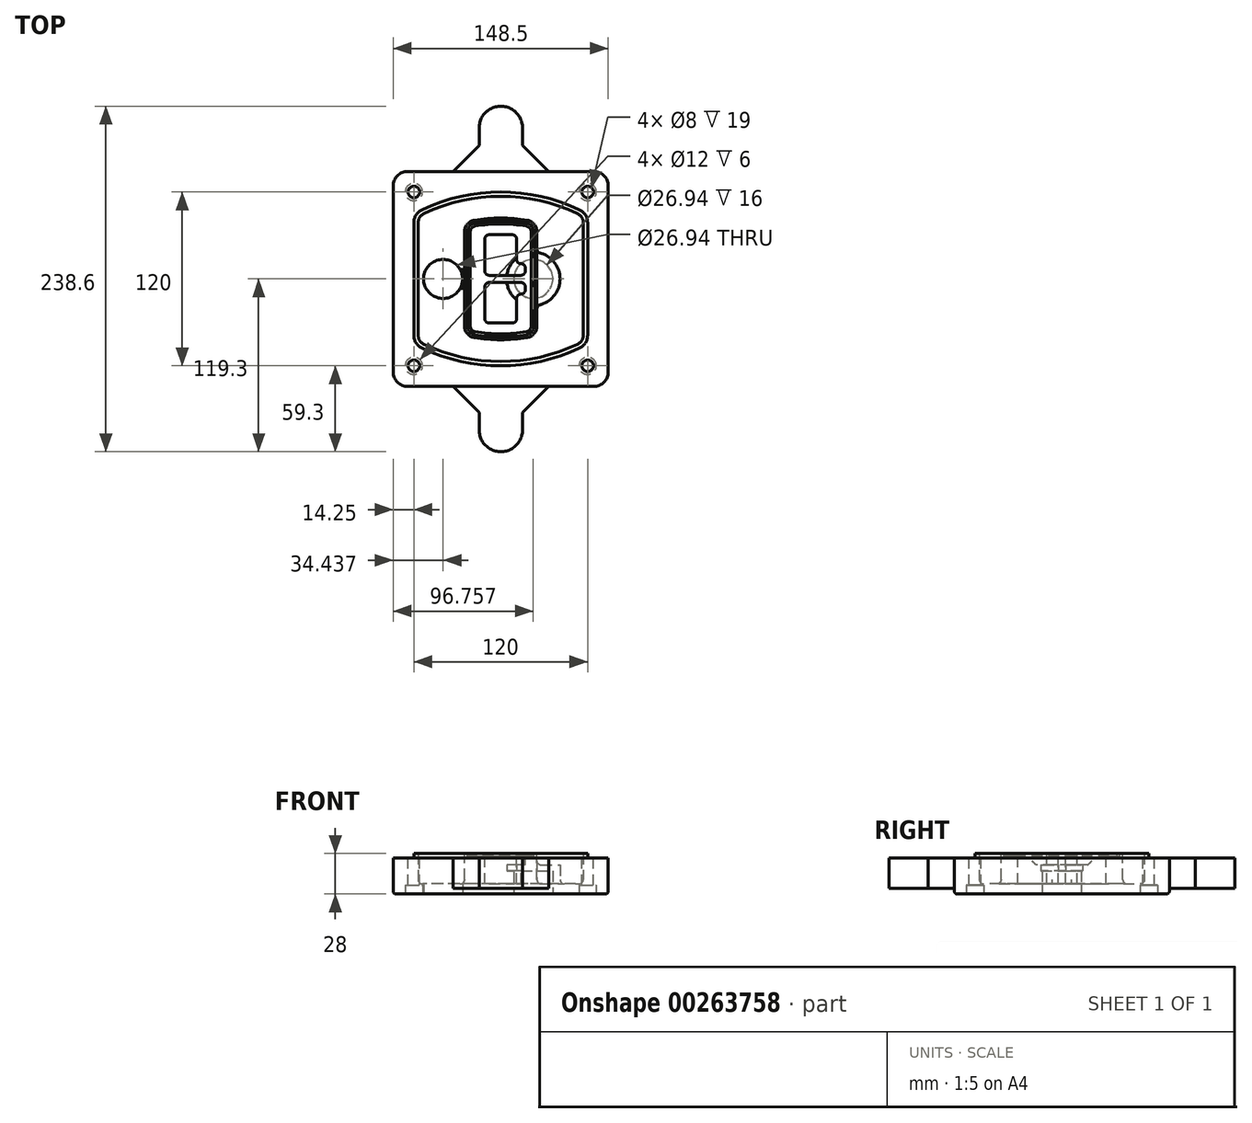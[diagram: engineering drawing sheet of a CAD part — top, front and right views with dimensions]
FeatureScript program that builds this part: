
annotation { "Feature Type Name" : "Feature", "Feature Type Description" : "" }
export const myFeature = defineFeature(function(context is Context, id is Id, definition is map)
    precondition{}
    {
        {
            var Q0;
            Q0=qCreatedBy(makeId("Top.planeOp"),FACE);
            var sketch = newSketch(context, id + "F0", { "sketchPlane" : qUnion([Q0])});
            skPoint(sketch, "E0.rect.middle", {"position": v(0, 0) * mm});
            skLineSegment(sketch, "E1.bottom", {"start": v(-64.25, -74.25) * mm, "end": v(64.25, -74.25) * mm});
            skLineSegment(sketch, "E1.top", {"start": v(-64.25, 74.25) * mm, "end": v(64.25, 74.25) * mm});
            skLineSegment(sketch, "E1.left", {"start": v(-74.25, -64.25) * mm, "end": v(-74.25, 64.25) * mm});
            skLineSegment(sketch, "E1.right", {"start": v(74.25, -64.25) * mm, "end": v(74.25, 64.25) * mm});
            skLineSegment(sketch, "E2", {"start": v(-74.25, 74.25) * mm, "end": v(74.25, -74.25) * mm, "construction": true});
            skLineSegment(sketch, "E3", {"start": v(74.25, 74.25) * mm, "end": v(-74.25, -74.25) * mm, "construction": true});
            skCircle(sketch, "E4", {"center": v(-60, 60) * mm, "radius": 4 * mm});
            skCircle(sketch, "E5", {"center": v(60, 60) * mm, "radius": 4 * mm});
            skCircle(sketch, "E6", {"center": v(60, -60) * mm, "radius": 4 * mm});
            skCircle(sketch, "E7", {"center": v(-60, -60) * mm, "radius": 4 * mm});
            skLineSegment(sketch, "E8", {"start": v(-60, 60) * mm, "end": v(60, 60) * mm, "construction": true});
            skLineSegment(sketch, "E9", {"start": v(60, 60) * mm, "end": v(60, -60) * mm, "construction": true});
            skLineSegment(sketch, "E10", {"start": v(60, -60) * mm, "end": v(-60, -60) * mm, "construction": true});
            skLineSegment(sketch, "E11", {"start": v(-60, -60) * mm, "end": v(-60, 60) * mm, "construction": true});
            skLineSegment(sketch, "E12", {"start": v(-60, 38.83) * mm, "end": v(-60, -38.83) * mm});
            skLineSegment(sketch, "E13", {"start": v(60, 38.83) * mm, "end": v(60, -38.83) * mm});
            skArc(sketch, "E14", {"start": v(54.26, 47.88) * mm, "mid": v(0, 60) * mm, "end": v(-54.26, 47.88) * mm});
            skArc(sketch, "E15", {"start": v(-54.26, -47.88) * mm, "mid": v(0, -60) * mm, "end": v(54.26, -47.88) * mm});
            skLineSegment(sketch, "E16", {"start": v(-60, 0) * mm, "end": v(60, 0) * mm, "construction": true});
            skPoint(sketch, "E17.visualSharp", {"position": v(-60, -45) * mm});
            skArc(sketch, "E17.filletArc", {"start": v(-60, -38.83) * mm, "mid": v(-58.44, -44.2) * mm, "end": v(-54.26, -47.88) * mm});
            skPoint(sketch, "E18.visualSharp", {"position": v(-60, 45) * mm});
            skArc(sketch, "E18.filletArc", {"start": v(-54.26, 47.88) * mm, "mid": v(-58.44, 44.2) * mm, "end": v(-60, 38.83) * mm});
            skPoint(sketch, "E19.visualSharp", {"position": v(60, 45) * mm});
            skArc(sketch, "E19.filletArc", {"start": v(60, 38.83) * mm, "mid": v(58.44, 44.2) * mm, "end": v(54.26, 47.88) * mm});
            skPoint(sketch, "E20.visualSharp", {"position": v(60, -45) * mm});
            skArc(sketch, "E20.filletArc", {"start": v(54.26, -47.88) * mm, "mid": v(58.44, -44.2) * mm, "end": v(60, -38.83) * mm});
            skPoint(sketch, "E21.visualSharp", {"position": v(-74.25, 74.25) * mm});
            skArc(sketch, "E21.filletArc", {"start": v(-64.25, 74.25) * mm, "mid": v(-71.32, 71.32) * mm, "end": v(-74.25, 64.25) * mm});
            skPoint(sketch, "E22.visualSharp", {"position": v(74.25, 74.25) * mm});
            skArc(sketch, "E22.filletArc", {"start": v(74.25, 64.25) * mm, "mid": v(71.32, 71.32) * mm, "end": v(64.25, 74.25) * mm});
            skPoint(sketch, "E23.visualSharp", {"position": v(74.25, -74.25) * mm});
            skArc(sketch, "E23.filletArc", {"start": v(64.25, -74.25) * mm, "mid": v(71.32, -71.32) * mm, "end": v(74.25, -64.25) * mm});
            skPoint(sketch, "E24.visualSharp", {"position": v(-74.25, -74.25) * mm});
            skArc(sketch, "E24.filletArc", {"start": v(-74.25, -64.25) * mm, "mid": v(-71.32, -71.32) * mm, "end": v(-64.25, -74.25) * mm});
            skArc(sketch, "E25.0", {"start": v(57, 38.83) * mm, "mid": v(55.9, 42.58) * mm, "end": v(52.98, 45.17) * mm});
            skLineSegment(sketch, "E25.1", {"start": v(57, 38.83) * mm, "end": v(57, -38.83) * mm});
            skArc(sketch, "E25.2", {"start": v(52.98, -45.17) * mm, "mid": v(55.9, -42.58) * mm, "end": v(57, -38.83) * mm});
            skArc(sketch, "E25.3", {"start": v(-52.98, -45.17) * mm, "mid": v(0, -57) * mm, "end": v(52.98, -45.17) * mm});
            skArc(sketch, "E25.4", {"start": v(-57, -38.83) * mm, "mid": v(-55.9, -42.58) * mm, "end": v(-52.98, -45.17) * mm});
            skArc(sketch, "E25.5", {"start": v(52.98, 45.17) * mm, "mid": v(0, 57) * mm, "end": v(-52.98, 45.17) * mm});
            skLineSegment(sketch, "E25.6", {"start": v(-57, 38.83) * mm, "end": v(-57, -38.83) * mm});
            skArc(sketch, "E25.7", {"start": v(-52.98, 45.17) * mm, "mid": v(-55.9, 42.58) * mm, "end": v(-57, 38.83) * mm});
            skArc(sketch, "E26.0", {"start": v(-55.96, 51.5) * mm, "mid": v(-61.82, 46.33) * mm, "end": v(-64, 38.83) * mm});
            skArc(sketch, "E26.1", {"start": v(55.96, 51.5) * mm, "mid": v(0, 64) * mm, "end": v(-55.96, 51.5) * mm});
            skArc(sketch, "E26.2", {"start": v(64, 38.83) * mm, "mid": v(61.82, 46.33) * mm, "end": v(55.96, 51.5) * mm});
            skLineSegment(sketch, "E26.3", {"start": v(64, 38.83) * mm, "end": v(64, -38.83) * mm});
            skArc(sketch, "E26.4", {"start": v(55.96, -51.5) * mm, "mid": v(61.82, -46.33) * mm, "end": v(64, -38.83) * mm});
            skLineSegment(sketch, "E26.5", {"start": v(-64, 38.83) * mm, "end": v(-64, -38.83) * mm});
            skArc(sketch, "E26.6", {"start": v(-55.96, -51.5) * mm, "mid": v(0, -64) * mm, "end": v(55.96, -51.5) * mm});
            skArc(sketch, "E26.7", {"start": v(-64, -38.83) * mm, "mid": v(-61.82, -46.33) * mm, "end": v(-55.96, -51.5) * mm});
            skSolve(sketch);
        }
        {
            var Q0;
            Q0=makeQuery(id+"F0.imprint","IMPRINT",FACE,{"disambiguationData":[TD([[makeQuery(id+"F0.imprint","IMPRINT",EDGE,{"derivedFrom":sQuery(id+"F0.wireOp",EDGE,"E1.bottom")}),1.0]])]});
            var Q1;
            Q1=makeQuery(id+"F0.imprint","IMPRINT",FACE,{"disambiguationData":[TD([[makeQuery(id+"F0.imprint","IMPRINT",EDGE,{"derivedFrom":sQuery(id+"F0.wireOp",EDGE,"E12")}),1.0]])]});
            var Q2;
            Q2=makeQuery(id+"F0.imprint","IMPRINT",FACE,{"disambiguationData":[TD([[makeQuery(id+"F0.imprint","IMPRINT",EDGE,{"derivedFrom":sQuery(id+"F0.wireOp",EDGE,"E25.0")}),1.0]])]});
            var Q3;
            Q3=makeQuery(id+"F0.imprint","IMPRINT",FACE,{"disambiguationData":[TD([[makeQuery(id+"F0.imprint","IMPRINT",EDGE,{"derivedFrom":sQuery(id+"F0.wireOp",EDGE,"E12")}),-1.0]])]});
            extrude(context, id + "F1", {"entities" : qUnion([Q0, Q1, Q2, Q3]), "oppositeDirection" : true, "depth" : 25 * mm});
        }
        {
            var Q0;
            Q0=makeQuery(id+"F0.imprint","IMPRINT",FACE,{"disambiguationData":[TD([[makeQuery(id+"F0.imprint","IMPRINT",EDGE,{"derivedFrom":sQuery(id+"F0.wireOp",EDGE,"E12")}),1.0]])]});
            extrude(context, id + "F2", {"entities" : qUnion([Q0]), "operationType" : NewBodyOperationType.ADD, "depth" : 3 * mm});
        }
        {
            var Q0;
            Q0=makeQuery(id+"F0.imprint","IMPRINT",FACE,{"disambiguationData":[TD([[makeQuery(id+"F0.imprint","IMPRINT",EDGE,{"derivedFrom":sQuery(id+"F0.wireOp",EDGE,"E25.0")}),1.0]])]});
            extrude(context, id + "F3", {"entities" : qUnion([Q0]), "operationType" : NewBodyOperationType.REMOVE, "oppositeDirection" : true, "depth" : 18 * mm});
        }
        {
            var Q0;
            Q0=makeQuery(id+"F2.opExtrude","CAP_FACE",FACE,{"disambiguationData":[OSD([sQuery(id+"F0.wireOp",EDGE,"E12"),sQuery(id+"F0.wireOp",EDGE,"E13"),sQuery(id+"F0.wireOp",EDGE,"E14"),sQuery(id+"F0.wireOp",EDGE,"E15"),sQuery(id+"F0.wireOp",EDGE,"E17.filletArc"),sQuery(id+"F0.wireOp",EDGE,"E18.filletArc"),sQuery(id+"F0.wireOp",EDGE,"E19.filletArc"),sQuery(id+"F0.wireOp",EDGE,"E20.filletArc"),sQuery(id+"F0.wireOp",EDGE,"E25.0"),sQuery(id+"F0.wireOp",EDGE,"E25.1"),sQuery(id+"F0.wireOp",EDGE,"E25.2"),sQuery(id+"F0.wireOp",EDGE,"E25.3"),sQuery(id+"F0.wireOp",EDGE,"E25.4"),sQuery(id+"F0.wireOp",EDGE,"E25.5"),sQuery(id+"F0.wireOp",EDGE,"E25.6"),sQuery(id+"F0.wireOp",EDGE,"E25.7")])],"isStart":false});
            var sketch = newSketch(context, id + "F4", { "sketchPlane" : qUnion([Q0])});
            skArc(sketch, "E27.0", {"start": v(-18.34, -40.45) * mm, "mid": v(0, -42) * mm, "end": v(18.34, -40.45) * mm});
            skArc(sketch, "E28.0", {"start": v(18.34, 40.45) * mm, "mid": v(0, 42) * mm, "end": v(-18.34, 40.45) * mm});
            skLineSegment(sketch, "E29", {"start": v(-25, 32.57) * mm, "end": v(-25, -32.57) * mm});
            skLineSegment(sketch, "E30", {"start": v(25, 32.57) * mm, "end": v(25, -32.57) * mm});
            skLineSegment(sketch, "E31", {"start": v(-25, 39.1) * mm, "end": v(25, 39.1) * mm, "construction": true});
            skLineSegment(sketch, "E32", {"start": v(-25, -39.1) * mm, "end": v(25, -39.1) * mm, "construction": true});
            skPoint(sketch, "E33.visualSharp", {"position": v(-25, 39.1) * mm});
            skArc(sketch, "E33.filletArc", {"start": v(-18.34, 40.45) * mm, "mid": v(-23.11, 37.73) * mm, "end": v(-25, 32.57) * mm});
            skPoint(sketch, "E34.visualSharp", {"position": v(25, 39.1) * mm});
            skArc(sketch, "E34.filletArc", {"start": v(25, 32.57) * mm, "mid": v(23.11, 37.73) * mm, "end": v(18.34, 40.45) * mm});
            skPoint(sketch, "E35.visualSharp", {"position": v(25, -39.1) * mm});
            skArc(sketch, "E35.filletArc", {"start": v(18.34, -40.45) * mm, "mid": v(23.11, -37.73) * mm, "end": v(25, -32.57) * mm});
            skPoint(sketch, "E36.visualSharp", {"position": v(-25, -39.1) * mm});
            skArc(sketch, "E36.filletArc", {"start": v(-25, -32.57) * mm, "mid": v(-23.11, -37.73) * mm, "end": v(-18.34, -40.45) * mm});
            skArc(sketch, "E37.0", {"start": v(52.98, 45.17) * mm, "mid": v(0, 57) * mm, "end": v(-52.98, 45.17) * mm});
            skArc(sketch, "E37.1", {"start": v(-52.98, 45.17) * mm, "mid": v(-55.9, 42.58) * mm, "end": v(-57, 38.83) * mm});
            skLineSegment(sketch, "E37.2", {"start": v(-57, 38.83) * mm, "end": v(-57, -38.83) * mm});
            skArc(sketch, "E37.3", {"start": v(-57, -38.83) * mm, "mid": v(-55.9, -42.58) * mm, "end": v(-52.98, -45.17) * mm});
            skArc(sketch, "E37.4", {"start": v(-52.98, -45.17) * mm, "mid": v(0, -57) * mm, "end": v(52.98, -45.17) * mm});
            skArc(sketch, "E37.5", {"start": v(52.98, -45.17) * mm, "mid": v(55.9, -42.58) * mm, "end": v(57, -38.83) * mm});
            skLineSegment(sketch, "E37.6", {"start": v(57, 38.83) * mm, "end": v(57, -38.83) * mm});
            skArc(sketch, "E37.7", {"start": v(57, 38.83) * mm, "mid": v(55.9, 42.58) * mm, "end": v(52.98, 45.17) * mm});
            skLineSegment(sketch, "E38.0", {"start": v(23, 32.57) * mm, "end": v(23, -32.57) * mm});
            skArc(sketch, "E38.1", {"start": v(18, -38.48) * mm, "mid": v(21.58, -36.44) * mm, "end": v(23, -32.57) * mm});
            skArc(sketch, "E38.2", {"start": v(-18, -38.48) * mm, "mid": v(0, -40) * mm, "end": v(18, -38.48) * mm});
            skArc(sketch, "E38.3", {"start": v(-23, -32.57) * mm, "mid": v(-21.58, -36.44) * mm, "end": v(-18, -38.48) * mm});
            skLineSegment(sketch, "E38.4", {"start": v(-23, 32.57) * mm, "end": v(-23, -32.57) * mm});
            skArc(sketch, "E38.5", {"start": v(23, 32.57) * mm, "mid": v(21.58, 36.44) * mm, "end": v(18, 38.48) * mm});
            skArc(sketch, "E38.6", {"start": v(-18, 38.48) * mm, "mid": v(-21.58, 36.44) * mm, "end": v(-23, 32.57) * mm});
            skArc(sketch, "E38.7", {"start": v(18, 38.48) * mm, "mid": v(0, 40) * mm, "end": v(-18, 38.48) * mm});
            skArc(sketch, "E39.0", {"start": v(21, 32.57) * mm, "mid": v(20.06, 35.15) * mm, "end": v(17.67, 36.5) * mm});
            skLineSegment(sketch, "E39.1", {"start": v(21, 32.57) * mm, "end": v(21, -32.57) * mm});
            skArc(sketch, "E39.2", {"start": v(17.67, -36.5) * mm, "mid": v(20.06, -35.15) * mm, "end": v(21, -32.57) * mm});
            skArc(sketch, "E39.3", {"start": v(-17.67, -36.5) * mm, "mid": v(0, -38) * mm, "end": v(17.67, -36.5) * mm});
            skArc(sketch, "E39.4", {"start": v(-21, -32.57) * mm, "mid": v(-20.06, -35.15) * mm, "end": v(-17.67, -36.5) * mm});
            skArc(sketch, "E39.5", {"start": v(17.67, 36.5) * mm, "mid": v(0, 38) * mm, "end": v(-17.67, 36.5) * mm});
            skLineSegment(sketch, "E39.6", {"start": v(-21, 32.57) * mm, "end": v(-21, -32.57) * mm});
            skArc(sketch, "E39.7", {"start": v(-17.67, 36.5) * mm, "mid": v(-20.06, 35.15) * mm, "end": v(-21, 32.57) * mm});
            skLineSegment(sketch, "E40", {"start": v(-25, 0) * mm, "end": v(25, 0) * mm, "construction": true});
            skLineSegment(sketch, "E41", {"start": v(-11, 5.5) * mm, "end": v(-11, 27.5) * mm});
            skLineSegment(sketch, "E42", {"start": v(-8, 30.5) * mm, "end": v(8, 30.5) * mm});
            skLineSegment(sketch, "E43", {"start": v(11, 27.5) * mm, "end": v(11, 13.5) * mm});
            skLineSegment(sketch, "E44", {"start": v(14, 10.5) * mm, "end": v(14, 10.5) * mm});
            skLineSegment(sketch, "E45", {"start": v(17, 7.5) * mm, "end": v(17, 5.5) * mm});
            skLineSegment(sketch, "E46", {"start": v(14, 2.5) * mm, "end": v(-8, 2.5) * mm});
            skPoint(sketch, "E47.visualSharp", {"position": v(-11, 30.5) * mm});
            skArc(sketch, "E47.filletArc", {"start": v(-8, 30.5) * mm, "mid": v(-10.12, 29.62) * mm, "end": v(-11, 27.5) * mm});
            skPoint(sketch, "E48.visualSharp", {"position": v(11, 30.5) * mm});
            skArc(sketch, "E48.filletArc", {"start": v(11, 27.5) * mm, "mid": v(10.12, 29.62) * mm, "end": v(8, 30.5) * mm});
            skPoint(sketch, "E49.visualSharp", {"position": v(11, 10.5) * mm});
            skArc(sketch, "E49.filletArc", {"start": v(11, 13.5) * mm, "mid": v(11.88, 11.38) * mm, "end": v(14, 10.5) * mm});
            skPoint(sketch, "E50.visualSharp", {"position": v(17, 10.5) * mm});
            skArc(sketch, "E50.filletArc", {"start": v(17, 7.5) * mm, "mid": v(16.12, 9.62) * mm, "end": v(14, 10.5) * mm});
            skPoint(sketch, "E51.visualSharp", {"position": v(17, 2.5) * mm});
            skArc(sketch, "E51.filletArc", {"start": v(14, 2.5) * mm, "mid": v(16.12, 3.38) * mm, "end": v(17, 5.5) * mm});
            skPoint(sketch, "E52.visualSharp", {"position": v(-11, 2.5) * mm});
            skArc(sketch, "E52.filletArc", {"start": v(-11, 5.5) * mm, "mid": v(-10.12, 3.38) * mm, "end": v(-8, 2.5) * mm});
            skLineSegment(sketch, "E53.0.MirrorCS", {"start": v(14, -2.5) * mm, "end": v(-8, -2.5) * mm});
            skArc(sketch, "E54.0.MirrorCS", {"start": v(-11, -5.5) * mm, "mid": v(-10.12, -3.38) * mm, "end": v(-8, -2.5) * mm});
            skLineSegment(sketch, "E55.0.MirrorCS", {"start": v(-11, -5.5) * mm, "end": v(-11, -27.5) * mm});
            skArc(sketch, "E56.0.MirrorCS", {"start": v(-8, -30.5) * mm, "mid": v(-10.12, -29.62) * mm, "end": v(-11, -27.5) * mm});
            skLineSegment(sketch, "E57.0.MirrorCS", {"start": v(-8, -30.5) * mm, "end": v(8, -30.5) * mm});
            skArc(sketch, "E58.0.MirrorCS", {"start": v(11, -27.5) * mm, "mid": v(10.12, -29.62) * mm, "end": v(8, -30.5) * mm});
            skLineSegment(sketch, "E59.0.MirrorCS", {"start": v(11, -27.5) * mm, "end": v(11, -13.5) * mm});
            skArc(sketch, "E60.0.MirrorCS", {"start": v(11, -13.5) * mm, "mid": v(11.88, -11.38) * mm, "end": v(14, -10.5) * mm});
            skArc(sketch, "E61.0.MirrorCS", {"start": v(17, -7.5) * mm, "mid": v(16.12, -9.62) * mm, "end": v(14, -10.5) * mm});
            skLineSegment(sketch, "E62.0.MirrorCS", {"start": v(17, -7.5) * mm, "end": v(17, -5.5) * mm});
            skArc(sketch, "E63.0.MirrorCS", {"start": v(14, -2.5) * mm, "mid": v(16.12, -3.38) * mm, "end": v(17, -5.5) * mm});
            skSolve(sketch);
        }
        {
            var Q0;
            Q0=makeQuery(id+"F4.imprint","IMPRINT",FACE,{"disambiguationData":[TD([[makeQuery(id+"F4.imprint","IMPRINT",EDGE,{"derivedFrom":sQuery(id+"F4.wireOp",EDGE,"E27.0")}),1.0]])]});
            var Q1;
            Q1=makeQuery(id+"F4.imprint","IMPRINT",FACE,{"disambiguationData":[TD([[makeQuery(id+"F4.imprint","IMPRINT",EDGE,{"derivedFrom":sQuery(id+"F4.wireOp",EDGE,"E38.0")}),-1.0]])]});
            var Q2;
            Q2=makeQuery(id+"F4.imprint","IMPRINT",FACE,{"disambiguationData":[TD([[makeQuery(id+"F4.imprint","IMPRINT",EDGE,{"derivedFrom":sQuery(id+"F4.wireOp",EDGE,"E39.0")}),1.0]])]});
            extrude(context, id + "F5", {"entities" : qUnion([Q0, Q1, Q2]), "operationType" : NewBodyOperationType.ADD, "endBound" : BoundingType.UP_TO_NEXT, "oppositeDirection" : true, "depth" : 25 * mm});
        }
        {
            var Q0;
            Q0=makeQuery(id+"F4.imprint","IMPRINT",FACE,{"disambiguationData":[TD([[makeQuery(id+"F4.imprint","IMPRINT",EDGE,{"derivedFrom":sQuery(id+"F4.wireOp",EDGE,"E38.0")}),-1.0]])]});
            extrude(context, id + "F6", {"entities" : qUnion([Q0]), "operationType" : NewBodyOperationType.REMOVE, "oppositeDirection" : true, "depth" : 2 * mm});
        }
        {
            var Q0;
            Q0=makeQuery(id+"F1.opExtrude","CAP_FACE",FACE,{"disambiguationData":[OSD([sQuery(id+"F0.wireOp",EDGE,"E1.bottom"),sQuery(id+"F0.wireOp",EDGE,"E1.top"),sQuery(id+"F0.wireOp",EDGE,"E1.left"),sQuery(id+"F0.wireOp",EDGE,"E1.right"),sQuery(id+"F0.wireOp",EDGE,"E4"),sQuery(id+"F0.wireOp",EDGE,"E5"),sQuery(id+"F0.wireOp",EDGE,"E6"),sQuery(id+"F0.wireOp",EDGE,"E7"),sQuery(id+"F0.wireOp",EDGE,"E21.filletArc"),sQuery(id+"F0.wireOp",EDGE,"E22.filletArc"),sQuery(id+"F0.wireOp",EDGE,"E23.filletArc"),sQuery(id+"F0.wireOp",EDGE,"E24.filletArc")])],"isStart":false});
            var sketch = newSketch(context, id + "F7", { "sketchPlane" : qUnion([Q0])});
            skCircle(sketch, "E64", {"center": v(22.5, 0) * mm, "radius": 13.47 * mm});
            skCircle(sketch, "E65", {"center": v(-39.81, 0) * mm, "radius": 13.47 * mm});
            skLineSegment(sketch, "E66", {"start": v(74.25, 0) * mm, "end": v(-74.25, 0) * mm});
            skCircle(sketch, "E67", {"center": v(22.5, 0) * mm, "radius": 18.47 * mm});
            skCircle(sketch, "E68", {"center": v(60, -60) * mm, "radius": 6 * mm});
            skCircle(sketch, "E69", {"center": v(-60, -60) * mm, "radius": 6 * mm});
            skCircle(sketch, "E70", {"center": v(-60, 60) * mm, "radius": 6 * mm});
            skCircle(sketch, "E71", {"center": v(60, 60) * mm, "radius": 6 * mm});
            skSolve(sketch);
        }
        {
            var Q0;
            {var subQ1=sQuery(id+"F7.wireOp",EDGE,"E66");var subQ4=sQuery(id+"F7.wireOp",EDGE,"E64");var subQ6=makeQuery(id+"F7.imprint","INTERSECT",VERTEX,{"disambiguationData":[OD(0.0)],"derivedFrom":[subQ4,subQ1]});Q0=makeQuery(id+"F7.imprint","IMPRINT",FACE,{"disambiguationData":[TD([[makeQuery(id+"F7.imprint","IMPRINT",EDGE,{"disambiguationData":[TD([[subQ6,-1.0]])],"derivedFrom":subQ4}),-1.0]])]});}
            var Q1;
            {var subQ0=sQuery(id+"F7.wireOp",EDGE,"E66");var subQ1=sQuery(id+"F7.wireOp",EDGE,"E64");var subQ3=makeQuery(id+"F7.imprint","INTERSECT",VERTEX,{"disambiguationData":[OD(0.0)],"derivedFrom":[subQ1,subQ0]});Q1=makeQuery(id+"F7.imprint","IMPRINT",FACE,{"disambiguationData":[TD([[makeQuery(id+"F7.imprint","IMPRINT",EDGE,{"disambiguationData":[TD([[subQ3,-1.0]])],"derivedFrom":subQ1}),1.0]])]});}
            var Q2;
            {var subQ0=sQuery(id+"F7.wireOp",EDGE,"E66");var subQ1=sQuery(id+"F7.wireOp",EDGE,"E64");var subQ3=makeQuery(id+"F7.imprint","INTERSECT",VERTEX,{"disambiguationData":[OD(0.0)],"derivedFrom":[subQ1,subQ0]});Q2=makeQuery(id+"F7.imprint","IMPRINT",FACE,{"disambiguationData":[TD([[makeQuery(id+"F7.imprint","IMPRINT",EDGE,{"disambiguationData":[TD([[subQ3,1.0]])],"derivedFrom":subQ1}),1.0]])]});}
            var Q3;
            {var subQ1=sQuery(id+"F7.wireOp",EDGE,"E66");var subQ4=sQuery(id+"F7.wireOp",EDGE,"E64");var subQ6=makeQuery(id+"F7.imprint","INTERSECT",VERTEX,{"disambiguationData":[OD(0.0)],"derivedFrom":[subQ4,subQ1]});Q3=makeQuery(id+"F7.imprint","IMPRINT",FACE,{"disambiguationData":[TD([[makeQuery(id+"F7.imprint","IMPRINT",EDGE,{"disambiguationData":[TD([[subQ6,1.0]])],"derivedFrom":subQ4}),-1.0]])]});}
            extrude(context, id + "F8", {"entities" : qUnion([Q0, Q1, Q2, Q3]), "operationType" : NewBodyOperationType.ADD, "oppositeDirection" : true, "depth" : 20 * mm});
        }
        {
            var Q0;
            {var subQ0=sQuery(id+"F7.wireOp",EDGE,"E66");var subQ1=sQuery(id+"F7.wireOp",EDGE,"E64");var subQ3=makeQuery(id+"F7.imprint","INTERSECT",VERTEX,{"disambiguationData":[OD(0.0)],"derivedFrom":[subQ1,subQ0]});Q0=makeQuery(id+"F7.imprint","IMPRINT",FACE,{"disambiguationData":[TD([[makeQuery(id+"F7.imprint","IMPRINT",EDGE,{"disambiguationData":[TD([[subQ3,-1.0]])],"derivedFrom":subQ1}),1.0]])]});}
            var Q1;
            {var subQ0=sQuery(id+"F7.wireOp",EDGE,"E66");var subQ1=sQuery(id+"F7.wireOp",EDGE,"E64");var subQ3=makeQuery(id+"F7.imprint","INTERSECT",VERTEX,{"disambiguationData":[OD(0.0)],"derivedFrom":[subQ1,subQ0]});Q1=makeQuery(id+"F7.imprint","IMPRINT",FACE,{"disambiguationData":[TD([[makeQuery(id+"F7.imprint","IMPRINT",EDGE,{"disambiguationData":[TD([[subQ3,1.0]])],"derivedFrom":subQ1}),1.0]])]});}
            extrude(context, id + "F9", {"entities" : qUnion([Q0, Q1]), "operationType" : NewBodyOperationType.REMOVE, "oppositeDirection" : true, "depth" : 16 * mm});
        }
        {
            var Q0;
            {var subQ0=sQuery(id+"F7.wireOp",EDGE,"E66");var subQ1=sQuery(id+"F7.wireOp",EDGE,"E65");var subQ3=makeQuery(id+"F7.imprint","INTERSECT",VERTEX,{"disambiguationData":[OD(0.0)],"derivedFrom":[subQ1,subQ0]});Q0=makeQuery(id+"F7.imprint","IMPRINT",FACE,{"disambiguationData":[TD([[makeQuery(id+"F7.imprint","IMPRINT",EDGE,{"disambiguationData":[TD([[subQ3,-1.0]])],"derivedFrom":subQ1}),1.0]])]});}
            var Q1;
            {var subQ0=sQuery(id+"F7.wireOp",EDGE,"E66");var subQ1=sQuery(id+"F7.wireOp",EDGE,"E65");var subQ3=makeQuery(id+"F7.imprint","INTERSECT",VERTEX,{"disambiguationData":[OD(0.0)],"derivedFrom":[subQ1,subQ0]});Q1=makeQuery(id+"F7.imprint","IMPRINT",FACE,{"disambiguationData":[TD([[makeQuery(id+"F7.imprint","IMPRINT",EDGE,{"disambiguationData":[TD([[subQ3,1.0]])],"derivedFrom":subQ1}),1.0]])]});}
            extrude(context, id + "F10", {"entities" : qUnion([Q0, Q1]), "operationType" : NewBodyOperationType.REMOVE, "oppositeDirection" : true, "depth" : 25 * mm});
        }
        {
            var Q0;
            Q0=makeQuery(id+"F7.imprint","IMPRINT",FACE,{"disambiguationData":[TD([[makeQuery(id+"F7.imprint","IMPRINT",EDGE,{"derivedFrom":sQuery(id+"F7.wireOp",EDGE,"E68")}),1.0]])]});
            var Q1;
            Q1=makeQuery(id+"F7.imprint","IMPRINT",FACE,{"disambiguationData":[TD([[makeQuery(id+"F7.imprint","IMPRINT",EDGE,{"derivedFrom":makeQuery(id+"F1.opExtrude","CAP_EDGE",EDGE,{"disambiguationData":[OSD([sQuery(id+"F0.wireOp",EDGE,"E5")])],"isStart":false})}),-1.0]])]});
            var Q2;
            Q2=makeQuery(id+"F7.imprint","IMPRINT",FACE,{"disambiguationData":[TD([[makeQuery(id+"F7.imprint","IMPRINT",EDGE,{"derivedFrom":sQuery(id+"F7.wireOp",EDGE,"E69")}),1.0]])]});
            var Q3;
            Q3=makeQuery(id+"F7.imprint","IMPRINT",FACE,{"disambiguationData":[TD([[makeQuery(id+"F7.imprint","IMPRINT",EDGE,{"derivedFrom":makeQuery(id+"F1.opExtrude","CAP_EDGE",EDGE,{"disambiguationData":[OSD([sQuery(id+"F0.wireOp",EDGE,"E4")])],"isStart":false})}),-1.0]])]});
            var Q4;
            Q4=makeQuery(id+"F7.imprint","IMPRINT",FACE,{"disambiguationData":[TD([[makeQuery(id+"F7.imprint","IMPRINT",EDGE,{"derivedFrom":sQuery(id+"F7.wireOp",EDGE,"E70")}),1.0]])]});
            var Q5;
            Q5=makeQuery(id+"F7.imprint","IMPRINT",FACE,{"disambiguationData":[TD([[makeQuery(id+"F7.imprint","IMPRINT",EDGE,{"derivedFrom":makeQuery(id+"F1.opExtrude","CAP_EDGE",EDGE,{"disambiguationData":[OSD([sQuery(id+"F0.wireOp",EDGE,"E7")])],"isStart":false})}),-1.0]])]});
            var Q6;
            Q6=makeQuery(id+"F7.imprint","IMPRINT",FACE,{"disambiguationData":[TD([[makeQuery(id+"F7.imprint","IMPRINT",EDGE,{"derivedFrom":sQuery(id+"F7.wireOp",EDGE,"E71")}),1.0]])]});
            var Q7;
            Q7=makeQuery(id+"F7.imprint","IMPRINT",FACE,{"disambiguationData":[TD([[makeQuery(id+"F7.imprint","IMPRINT",EDGE,{"derivedFrom":makeQuery(id+"F1.opExtrude","CAP_EDGE",EDGE,{"disambiguationData":[OSD([sQuery(id+"F0.wireOp",EDGE,"E6")])],"isStart":false})}),-1.0]])]});
            extrude(context, id + "F11", {"entities" : qUnion([Q0, Q1, Q2, Q3, Q4, Q5, Q6, Q7]), "operationType" : NewBodyOperationType.REMOVE, "oppositeDirection" : true, "depth" : 6 * mm});
        }
        {
            var Q0;
            Q0=makeQuery(id+"F9.boolean.opBoolean","COPY",FACE,{"derivedFrom":makeQuery(id+"F9.opExtrude","CAP_FACE",FACE,{"disambiguationData":[OSD([sQuery(id+"F7.wireOp",EDGE,"E64")])],"isStart":false})});
            var sketch = newSketch(context, id + "F12", { "sketchPlane" : qUnion([Q0])});
            skArc(sketch, "E72.0", {"start": v(11, 14.45) * mm, "mid": v(6.45, 9.13) * mm, "end": v(4.2, 2.5) * mm});
            skArc(sketch, "E72.1", {"start": v(4.2, -2.5) * mm, "mid": v(6.45, -9.13) * mm, "end": v(11, -14.45) * mm});
            skLineSegment(sketch, "E73", {"start": v(4.2, -2.5) * mm, "end": v(14, -2.5) * mm});
            skLineSegment(sketch, "E74.0", {"start": v(14, 2.5) * mm, "end": v(4.2, 2.5) * mm});
            skArc(sketch, "E74.1", {"start": v(14, 2.5) * mm, "mid": v(16.12, 3.38) * mm, "end": v(17, 5.5) * mm});
            skLineSegment(sketch, "E74.2", {"start": v(17, 7.5) * mm, "end": v(17, 5.5) * mm});
            skArc(sketch, "E74.3", {"start": v(17, 7.5) * mm, "mid": v(16.12, 9.62) * mm, "end": v(14, 10.5) * mm});
            skArc(sketch, "E74.4", {"start": v(11, 13.5) * mm, "mid": v(11.88, 11.38) * mm, "end": v(14, 10.5) * mm});
            skLineSegment(sketch, "E74.5", {"start": v(11, 14.45) * mm, "end": v(11, 13.5) * mm});
            skLineSegment(sketch, "E74.7", {"start": v(14, -2.5) * mm, "end": v(4.2, -2.5) * mm});
            skArc(sketch, "E74.8", {"start": v(14, -2.5) * mm, "mid": v(16.12, -3.38) * mm, "end": v(17, -5.5) * mm});
            skLineSegment(sketch, "E74.9", {"start": v(17, -7.5) * mm, "end": v(17, -5.5) * mm});
            skArc(sketch, "E74.10", {"start": v(17, -7.5) * mm, "mid": v(16.12, -9.62) * mm, "end": v(14, -10.5) * mm});
            skArc(sketch, "E74.11", {"start": v(11, -13.5) * mm, "mid": v(11.88, -11.38) * mm, "end": v(14, -10.5) * mm});
            skLineSegment(sketch, "E74.12", {"start": v(11, -14.45) * mm, "end": v(11, -13.5) * mm});
            skPoint(sketch, "E75.orphan", {"position": v(11, -27.5) * mm});
            skPoint(sketch, "E76.orphan", {"position": v(-8, -2.5) * mm});
            skPoint(sketch, "E77.orphan", {"position": v(-8, 2.5) * mm});
            skPoint(sketch, "E78.orphan", {"position": v(11, 27.5) * mm});
            skSolve(sketch);
        }
        {
            var Q0;
            {var subQ7=sQuery(id+"F12.wireOp",EDGE,"E72.0");var subQ14=sQuery(id+"F12.wireOp",EDGE,"E72.1");var subQ16=sQuery(id+"F12.wireOp",EDGE,"E74.1");var subQ18=sQuery(id+"F12.wireOp",EDGE,"E74.8");Q0=qUnion([makeQuery(id+"F12.imprint","IMPRINT",FACE,{"disambiguationData":[TD([[makeQuery(id+"F12.imprint","IMPRINT",EDGE,{"derivedFrom":subQ7}),1.0]])]}),makeQuery(id+"F12.imprint","IMPRINT",FACE,{"disambiguationData":[TD([[makeQuery(id+"F12.imprint","IMPRINT",EDGE,{"derivedFrom":subQ14}),1.0]])]}),makeQuery(id+"F12.imprint","IMPRINT",FACE,{"disambiguationData":[TD([[makeQuery(id+"F12.imprint","IMPRINT",EDGE,{"derivedFrom":subQ16}),1.0]])]}),makeQuery(id+"F12.imprint","IMPRINT",FACE,{"disambiguationData":[TD([[makeQuery(id+"F12.imprint","IMPRINT",EDGE,{"derivedFrom":subQ18}),-1.0]])]})]);}
            var Q1;
            Q1=makeQuery(id+"F5.boolean.opBoolean","SPLIT",FACE,{"disambiguationData":[TD([makeQuery(id+"F5.opExtrude","SWEPT_FACE",FACE,{"disambiguationData":[OSD([sQuery(id+"F4.wireOp",EDGE,"E41")])]})])],"derivedFrom":makeQuery(id+"F3.boolean.opBoolean","COPY",FACE,{"derivedFrom":makeQuery(id+"F3.opExtrude","CAP_FACE",FACE,{"disambiguationData":[OSD([sQuery(id+"F0.wireOp",EDGE,"E25.0"),sQuery(id+"F0.wireOp",EDGE,"E25.1"),sQuery(id+"F0.wireOp",EDGE,"E25.2"),sQuery(id+"F0.wireOp",EDGE,"E25.3"),sQuery(id+"F0.wireOp",EDGE,"E25.4"),sQuery(id+"F0.wireOp",EDGE,"E25.5"),sQuery(id+"F0.wireOp",EDGE,"E25.6"),sQuery(id+"F0.wireOp",EDGE,"E25.7")])],"isStart":false})})});
            extrude(context, id + "F13", {"entities" : qUnion([Q0]), "operationType" : NewBodyOperationType.REMOVE, "endBound" : BoundingType.UP_TO_SURFACE, "endBoundEntityFace" : qUnion([Q1]), "depth" : 25 * mm});
        }
        {
            var Q0;
            Q0=makeQuery(id+"F3.boolean.opBoolean","COPY",EDGE,{"derivedFrom":makeQuery(id+"F3.opExtrude","CAP_EDGE",EDGE,{"disambiguationData":[OSD([sQuery(id+"F0.wireOp",EDGE,"E25.6")])],"isStart":false})});
            var Q1;
            Q1=makeQuery(id+"F8.boolean.opBoolean","INTERSECT",EDGE,{"derivedFrom":[makeQuery(id+"F5.opExtrude","SWEPT_FACE",FACE,{"disambiguationData":[OSD([sQuery(id+"F4.wireOp",EDGE,"E30")])]}),makeQuery(id+"F8.opExtrude","CAP_FACE",FACE,{"disambiguationData":[OSD([sQuery(id+"F7.wireOp",EDGE,"E67")])],"isStart":false})]});
            var Q2;
            Q2=makeQuery(id+"F8.boolean.opBoolean","INTERSECT",EDGE,{"disambiguationData":[OD(1.0)],"derivedFrom":[makeQuery(id+"F5.opExtrude","SWEPT_FACE",FACE,{"disambiguationData":[OSD([sQuery(id+"F4.wireOp",EDGE,"E30")])]}),makeQuery(id+"F8.opExtrude","SWEPT_FACE",FACE,{"disambiguationData":[OSD([sQuery(id+"F7.wireOp",EDGE,"E67")])]})]});
            var Q3;
            {var subQ0=sQuery(id+"F4.wireOp",EDGE,"E30");Q3=makeQuery(id+"F8.boolean.opBoolean","SPLIT",EDGE,{"disambiguationData":[TD([makeQuery(id+"F5.opExtrude","SWEPT_FACE",FACE,{"disambiguationData":[OSD([sQuery(id+"F4.wireOp",EDGE,"E35.filletArc")])]})])],"derivedFrom":makeQuery(id+"F5.opExtrude","CAP_EDGE",EDGE,{"disambiguationData":[OSD([subQ0])],"isStart":false})});}
            var Q4;
            {var subQ0=sQuery(id+"F0.wireOp",EDGE,"E25.7");var subQ1=sQuery(id+"F0.wireOp",EDGE,"E25.1");var subQ2=sQuery(id+"F0.wireOp",EDGE,"E25.6");var subQ3=sQuery(id+"F0.wireOp",EDGE,"E25.5");var subQ4=sQuery(id+"F0.wireOp",EDGE,"E25.4");var subQ5=sQuery(id+"F0.wireOp",EDGE,"E25.0");var subQ6=sQuery(id+"F0.wireOp",EDGE,"E25.2");var subQ7=sQuery(id+"F0.wireOp",EDGE,"E25.3");Q4=makeQuery(id+"F8.boolean.opBoolean","INTERSECT",EDGE,{"derivedFrom":[makeQuery(id+"F5.boolean.opBoolean","SPLIT",FACE,{"disambiguationData":[TD([makeQuery(id+"F2.opExtrude","SWEPT_FACE",FACE,{"disambiguationData":[OSD([subQ5])]})])],"derivedFrom":makeQuery(id+"F3.boolean.opBoolean","COPY",FACE,{"derivedFrom":makeQuery(id+"F3.opExtrude","CAP_FACE",FACE,{"disambiguationData":[OSD([subQ5,subQ1,subQ6,subQ7,subQ4,subQ3,subQ2,subQ0])],"isStart":false})})}),makeQuery(id+"F8.opExtrude","SWEPT_FACE",FACE,{"disambiguationData":[OSD([sQuery(id+"F7.wireOp",EDGE,"E67")])]})]});}
            var Q5;
            Q5=makeQuery(id+"F8.boolean.opBoolean","INTERSECT",EDGE,{"disambiguationData":[OD(0.0)],"derivedFrom":[makeQuery(id+"F5.opExtrude","SWEPT_FACE",FACE,{"disambiguationData":[OSD([sQuery(id+"F4.wireOp",EDGE,"E30")])]}),makeQuery(id+"F8.opExtrude","SWEPT_FACE",FACE,{"disambiguationData":[OSD([sQuery(id+"F7.wireOp",EDGE,"E67")])]})]});
            fillet(context, id + "F14", {"entities" : qUnion([Q0, Q1, Q2, Q3, Q4, Q5]), "radius" : 3 * mm, "tangentPropagation" : true, "allowEdgeOverflow" : false});
        }
        {
            var Q0;
            Q0=makeQuery(id+"F1.opExtrude","CAP_EDGE",EDGE,{"disambiguationData":[OSD([sQuery(id+"F0.wireOp",EDGE,"E1.bottom")])],"isStart":false});
            fillet(context, id + "F15", {"entities" : qUnion([Q0]), "radius" : 2 * mm, "tangentPropagation" : true, "allowEdgeOverflow" : false});
        }
        {
            var Q0;
            {var subQ0=sQuery(id+"F0.wireOp",EDGE,"E21.filletArc");var subQ1=sQuery(id+"F0.wireOp",EDGE,"E7");var subQ2=sQuery(id+"F0.wireOp",EDGE,"E6");var subQ3=sQuery(id+"F0.wireOp",EDGE,"E5");var subQ4=sQuery(id+"F0.wireOp",EDGE,"E4");var subQ5=sQuery(id+"F0.wireOp",EDGE,"E22.filletArc");var subQ6=sQuery(id+"F0.wireOp",EDGE,"E1.bottom");var subQ7=sQuery(id+"F0.wireOp",EDGE,"E1.right");var subQ8=sQuery(id+"F0.wireOp",EDGE,"E1.top");var subQ9=sQuery(id+"F0.wireOp",EDGE,"E1.left");var subQ10=sQuery(id+"F0.wireOp",EDGE,"E23.filletArc");var subQ11=sQuery(id+"F0.wireOp",EDGE,"E24.filletArc");Q0=makeQuery(id+"F2.boolean.opBoolean","SPLIT",FACE,{"disambiguationData":[TD([makeQuery(id+"F1.opExtrude","SWEPT_FACE",FACE,{"disambiguationData":[OSD([subQ6])]})])],"derivedFrom":makeQuery(id+"F1.opExtrude","CAP_FACE",FACE,{"disambiguationData":[OSD([subQ6,subQ8,subQ9,subQ7,subQ4,subQ3,subQ2,subQ1,subQ0,subQ5,subQ10,subQ11])],"isStart":true})});}
            var sketch = newSketch(context, id + "F16", { "sketchPlane" : qUnion([Q0])});
            skCircle(sketch, "E79", {"center": v(0, 104.25) * mm, "radius": 6 * mm});
            skLineSegment(sketch, "E80", {"start": v(0, 104.25) * mm, "end": v(0, 74.25) * mm, "construction": true});
            skArc(sketch, "E81", {"start": v(15.08, 104.25) * mm, "mid": v(0.08, 119.3) * mm, "end": v(-14.92, 104.25) * mm});
            skLineSegment(sketch, "E82", {"start": v(-14.92, 104.25) * mm, "end": v(-14.88, 92.25) * mm});
            skLineSegment(sketch, "E83", {"start": v(-32.88, 74.25) * mm, "end": v(-14.88, 92.25) * mm});
            skLineSegment(sketch, "E84", {"start": v(15.08, 104.25) * mm, "end": v(15.08, 92.25) * mm});
            skLineSegment(sketch, "E85", {"start": v(15.08, 92.25) * mm, "end": v(33.08, 74.25) * mm});
            skLineSegment(sketch, "E86", {"start": v(-74.25, 0) * mm, "end": v(111.73, 0) * mm, "construction": true});
            skPoint(sketch, "E86.endSnap0", {"position": v(-74.25, 0) * mm});
            skLineSegment(sketch, "E87.MirrorCS", {"start": v(-32.88, -74.25) * mm, "end": v(-14.88, -92.25) * mm});
            skLineSegment(sketch, "E88.MirrorCS", {"start": v(-14.92, -104.25) * mm, "end": v(-14.88, -92.25) * mm});
            skLineSegment(sketch, "E89.MirrorCS", {"start": v(15.08, -104.25) * mm, "end": v(15.08, -92.25) * mm});
            skLineSegment(sketch, "E90.MirrorCS", {"start": v(15.08, -92.25) * mm, "end": v(33.08, -74.25) * mm});
            skArc(sketch, "E91.MirrorCS", {"start": v(15.08, -104.25) * mm, "mid": v(0.08, -119.3) * mm, "end": v(-14.92, -104.25) * mm});
            skCircle(sketch, "E92.MirrorC", {"center": v(0, -104.25) * mm, "radius": 6 * mm});
            skSolve(sketch);
        }
        {
            var Q0;
            Q0 = qSketchRegion(id + "F16", true);
            var Q1;
            {var subQ1=sQuery(id+"F16.wireOp",EDGE,"E87.MirrorCS");Q1=makeQuery(id+"F16.imprint","IMPRINT",FACE,{"disambiguationData":[TD([[makeQuery(id+"F16.imprint","IMPRINT",EDGE,{"derivedFrom":subQ1}),1.0]])]});}
            var Q2;
            Q2=makeQuery(id+"F16.imprint","IMPRINT",FACE,{"disambiguationData":[TD([[makeQuery(id+"F16.imprint","IMPRINT",EDGE,{"derivedFrom":sQuery(id+"F16.wireOp",EDGE,"E79")}),-1.0]])]});
            var Q3;
            {var subQ0=sQuery(id+"F0.wireOp",EDGE,"E21.filletArc");var subQ1=sQuery(id+"F0.wireOp",EDGE,"E7");var subQ2=sQuery(id+"F0.wireOp",EDGE,"E6");var subQ3=sQuery(id+"F0.wireOp",EDGE,"E5");var subQ4=sQuery(id+"F0.wireOp",EDGE,"E4");var subQ5=sQuery(id+"F0.wireOp",EDGE,"E22.filletArc");var subQ6=sQuery(id+"F0.wireOp",EDGE,"E1.bottom");var subQ7=sQuery(id+"F0.wireOp",EDGE,"E1.right");var subQ8=sQuery(id+"F0.wireOp",EDGE,"E1.top");var subQ9=sQuery(id+"F0.wireOp",EDGE,"E1.left");var subQ10=sQuery(id+"F0.wireOp",EDGE,"E23.filletArc");var subQ11=sQuery(id+"F0.wireOp",EDGE,"E24.filletArc");Q3=makeQuery(id+"F2.boolean.opBoolean","SPLIT",FACE,{"disambiguationData":[TD([makeQuery(id+"F1.opExtrude","SWEPT_FACE",FACE,{"disambiguationData":[OSD([subQ6])]})])],"derivedFrom":makeQuery(id+"F1.opExtrude","CAP_FACE",FACE,{"disambiguationData":[OSD([subQ6,subQ8,subQ9,subQ7,subQ4,subQ3,subQ2,subQ1,subQ0,subQ5,subQ10,subQ11])],"isStart":true})});}
            extrude(context, id + "F17", {"entities" : qUnion([Q0, Q1, Q2]), "oppositeDirection" : true, "endBoundEntityFace" : qUnion([Q3]), "depth" : 21 * mm});
        }
    });
